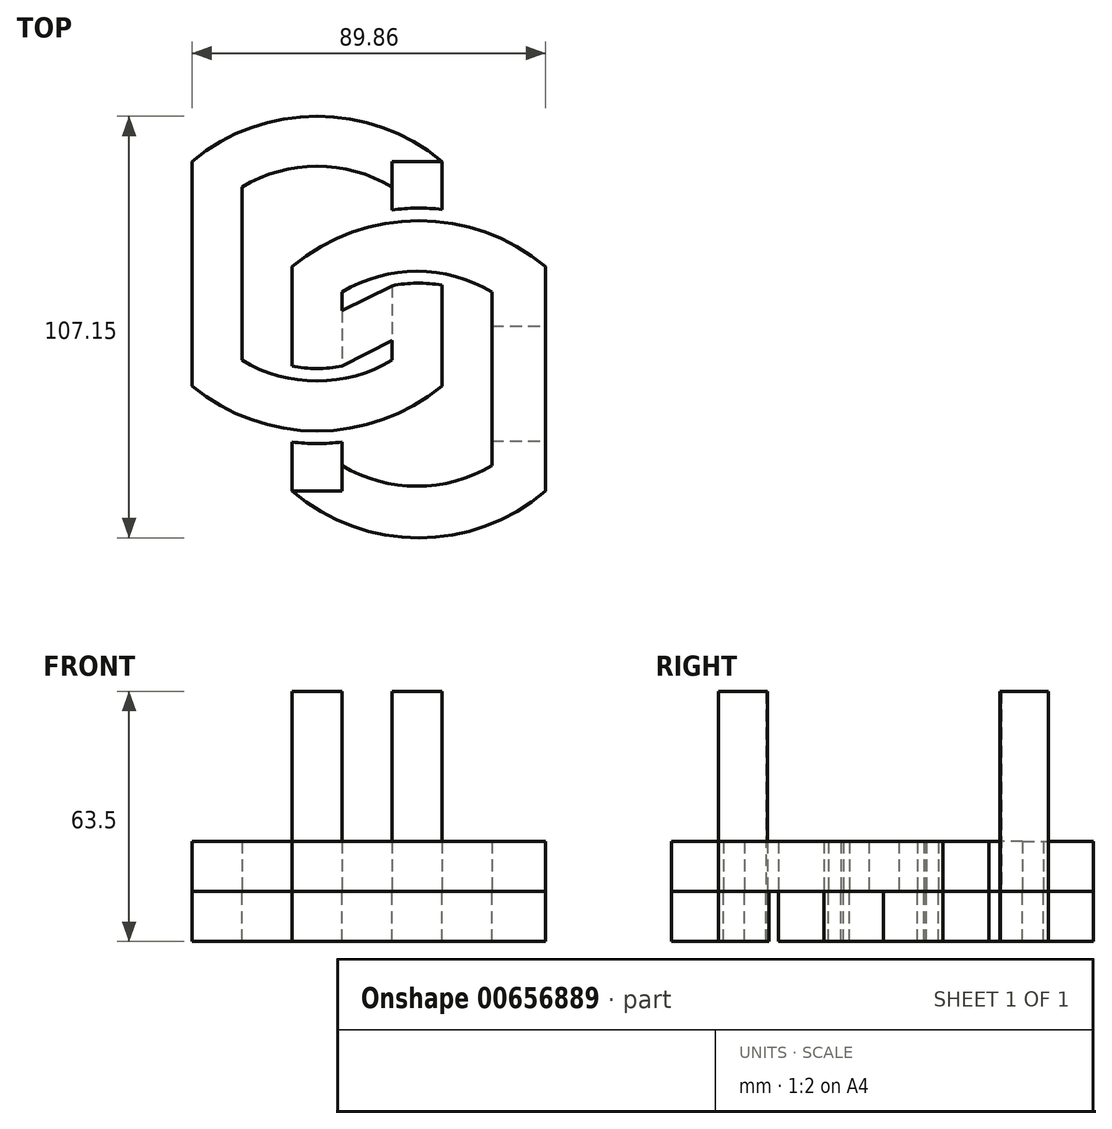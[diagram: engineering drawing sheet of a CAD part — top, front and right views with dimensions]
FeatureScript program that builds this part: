
annotation { "Feature Type Name" : "Feature", "Feature Type Description" : "" }
export const myFeature = defineFeature(function(context is Context, id is Id, definition is map)
    precondition{}
    {
        {
            var Q0;
            Q0=qCreatedBy(makeId("Top.planeOp"),FACE);
            var sketch = newSketch(context, id + "F0", { "sketchPlane" : qUnion([Q0])});
            skLineSegment(sketch, "E0.0", {"start": v(-60.44, 47.14) * mm, "end": v(-60.44, -9.85) * mm});
            skArc(sketch, "E1.0", {"start": v(-47.74, -3.35) * mm, "mid": v(-28.7, -8.66) * mm, "end": v(-9.64, -3.35) * mm});
            skArc(sketch, "E2.0", {"start": v(-60.44, -9.85) * mm, "mid": v(-28.7, -21.36) * mm, "end": v(3.06, -9.85) * mm});
            skArc(sketch, "E3.0", {"start": v(3.06, 47.14) * mm, "mid": v(-28.7, 58.65) * mm, "end": v(-60.44, 47.14) * mm});
            skArc(sketch, "E4.0", {"start": v(-9.64, 40.65) * mm, "mid": v(-28.7, 45.95) * mm, "end": v(-47.74, 40.65) * mm});
            skLineSegment(sketch, "E5.0", {"start": v(-47.74, 40.65) * mm, "end": v(-47.74, -3.35) * mm});
            skLineSegment(sketch, "E6.0", {"start": v(-9.64, 40.65) * mm, "end": v(-9.64, 34.84) * mm});
            skLineSegment(sketch, "E7.0", {"start": v(3.06, 47.14) * mm, "end": v(3.06, 34.96) * mm});
            skLineSegment(sketch, "E8.0.1.0", {"start": v(-35.05, 20.42) * mm, "end": v(-35.05, -4.88) * mm});
            skArc(sketch, "E8.0.1.1", {"start": v(-35.05, -36.58) * mm, "mid": v(-2.81, -48.5) * mm, "end": v(29.42, -36.58) * mm});
            skArc(sketch, "E8.0.1.2", {"start": v(-22.34, -30.07) * mm, "mid": v(-3.3, -35.38) * mm, "end": v(15.76, -30.07) * mm});
            skArc(sketch, "E8.0.1.5", {"start": v(15.76, 13.93) * mm, "mid": v(-3.3, 19.23) * mm, "end": v(-22.34, 13.93) * mm});
            skArc(sketch, "E8.0.1.6", {"start": v(29.42, 20.42) * mm, "mid": v(-2.81, 32.1) * mm, "end": v(-35.05, 20.42) * mm});
            skLineSegment(sketch, "E8.0.1.7", {"start": v(-22.34, 13.93) * mm, "end": v(-22.34, -4.88) * mm});
            skLineSegment(sketch, "E8.0.1.8", {"start": v(29.42, 20.42) * mm, "end": v(29.42, 5.28) * mm});
            skLineSegment(sketch, "E8.0.1.9", {"start": v(15.76, 13.93) * mm, "end": v(15.76, 5.28) * mm});
            skLineSegment(sketch, "E9", {"start": v(15.76, 5.28) * mm, "end": v(29.42, 5.28) * mm});
            skLineSegment(sketch, "E10", {"start": v(15.76, -23.85) * mm, "end": v(29.42, -23.85) * mm});
            skLineSegment(sketch, "E11.trimOffspring", {"start": v(15.76, -23.85) * mm, "end": v(15.76, -30.07) * mm});
            skLineSegment(sketch, "E12.trimOffspring", {"start": v(29.42, -23.85) * mm, "end": v(29.42, -36.58) * mm});
            skArc(sketch, "E13.0", {"start": v(3.06, 34.96) * mm, "mid": v(-3.3, 35.28) * mm, "end": v(-9.64, 34.84) * mm});
            skArc(sketch, "E14.0", {"start": v(3.06, 15.72) * mm, "mid": v(-3.3, 16.23) * mm, "end": v(-9.64, 15.54) * mm});
            skLineSegment(sketch, "E15.trimOffspring", {"start": v(3.06, 15.72) * mm, "end": v(3.06, -9.85) * mm});
            skLineSegment(sketch, "E16.trimOffspring", {"start": v(-9.64, 15.54) * mm, "end": v(-9.64, -3.35) * mm});
            skArc(sketch, "E17.0", {"start": v(-35.05, -4.88) * mm, "mid": v(-28.7, -5.48) * mm, "end": v(-22.34, -4.88) * mm});
            skArc(sketch, "E18.0", {"start": v(-35.05, -24.15) * mm, "mid": v(-28.7, -24.53) * mm, "end": v(-22.34, -24.15) * mm});
            skLineSegment(sketch, "E19.trimOffspring", {"start": v(-35.05, -24.15) * mm, "end": v(-35.05, -36.58) * mm});
            skLineSegment(sketch, "E20.trimOffspring", {"start": v(-22.34, -24.15) * mm, "end": v(-22.34, -30.07) * mm});
            skLineSegment(sketch, "E21", {"start": v(-22.34, 9.21) * mm, "end": v(-9.64, 15.54) * mm});
            skLineSegment(sketch, "E22", {"start": v(-22.34, -4.88) * mm, "end": v(-9.64, 1.64) * mm});
            skLineSegment(sketch, "E23.left", {"start": v(15.76, -23.85) * mm, "end": v(15.76, 5.28) * mm});
            skLineSegment(sketch, "E23.right", {"start": v(29.42, -23.85) * mm, "end": v(29.42, 5.28) * mm});
            skLineSegment(sketch, "E24.top", {"start": v(-22.34, -36.58) * mm, "end": v(-35.05, -36.58) * mm});
            skLineSegment(sketch, "E24.left", {"start": v(-22.34, -24.15) * mm, "end": v(-22.34, -36.58) * mm});
            skLineSegment(sketch, "E25.top", {"start": v(-9.64, 47.14) * mm, "end": v(3.06, 47.14) * mm});
            skLineSegment(sketch, "E25.left", {"start": v(-9.64, 34.84) * mm, "end": v(-9.64, 47.14) * mm});
            skLineSegment(sketch, "E25.right", {"start": v(3.06, 34.84) * mm, "end": v(3.06, 47.14) * mm});
            skSolve(sketch);
        }
        {
            var Q0;
            Q0=makeQuery(id+"F0.imprint","IMPRINT",FACE,{"disambiguationData":[TD([[makeQuery(id+"F0.imprint","IMPRINT",EDGE,{"derivedFrom":sQuery(id+"F0.wireOp",EDGE,"E0.0")}),1.0]])]});
            var Q1;
            Q1=makeQuery(id+"F0.imprint","IMPRINT",FACE,{"disambiguationData":[TD([[makeQuery(id+"F0.imprint","IMPRINT",EDGE,{"derivedFrom":sQuery(id+"F0.wireOp",EDGE,"E8.0.1.0")}),1.0]])]});
            var Q2;
            Q2=makeQuery(id+"F0.imprint","IMPRINT",FACE,{"disambiguationData":[TD([[makeQuery(id+"F0.imprint","IMPRINT",EDGE,{"derivedFrom":sQuery(id+"F0.wireOp",EDGE,"E8.0.1.1")}),1.0]])]});
            var Q3;
            {var subQ2=sQuery(id+"F0.wireOp",EDGE,"E18.0");Q3=makeQuery(id+"F0.imprint","IMPRINT",FACE,{"disambiguationData":[TD([[makeQuery(id+"F0.imprint","IMPRINT",EDGE,{"derivedFrom":subQ2}),-1.0]])]});}
            var Q4;
            {var subQ2=sQuery(id+"F0.wireOp",EDGE,"E13.0");Q4=makeQuery(id+"F0.imprint","IMPRINT",FACE,{"disambiguationData":[TD([[makeQuery(id+"F0.imprint","IMPRINT",EDGE,{"derivedFrom":subQ2}),-1.0]])]});}
            extrude(context, id + "F1", {"entities" : qUnion([Q0, Q1, Q2, Q3, Q4]), "depth" : -12.7 * mm, "offsetDistance" : 25.4 * mm});
        }
        {
            var Q0;
            {var subQ2=sQuery(id+"F0.wireOp",EDGE,"E13.0");Q0=makeQuery(id+"F0.imprint","IMPRINT",FACE,{"disambiguationData":[TD([[makeQuery(id+"F0.imprint","IMPRINT",EDGE,{"derivedFrom":subQ2}),-1.0]])]});}
            var Q1;
            {var subQ2=sQuery(id+"F0.wireOp",EDGE,"E18.0");Q1=makeQuery(id+"F0.imprint","IMPRINT",FACE,{"disambiguationData":[TD([[makeQuery(id+"F0.imprint","IMPRINT",EDGE,{"derivedFrom":subQ2}),-1.0]])]});}
            extrude(context, id + "F2", {"entities" : qUnion([Q0, Q1]), "depth" : 50.8 * mm, "offsetDistance" : 25.4 * mm});
        }
        {
            var Q0;
            Q0=makeQuery(id+"F0.imprint","IMPRINT",FACE,{"disambiguationData":[TD([[makeQuery(id+"F0.imprint","IMPRINT",EDGE,{"derivedFrom":sQuery(id+"F0.wireOp",EDGE,"E0.0")}),1.0]])]});
            var Q1;
            Q1=makeQuery(id+"F0.imprint","IMPRINT",FACE,{"disambiguationData":[TD([[makeQuery(id+"F0.imprint","IMPRINT",EDGE,{"derivedFrom":sQuery(id+"F0.wireOp",EDGE,"E8.0.1.0")}),1.0]])]});
            var Q2;
            {var subQ2=sQuery(id+"F0.wireOp",EDGE,"E21");Q2=makeQuery(id+"F0.imprint","IMPRINT",FACE,{"disambiguationData":[TD([[makeQuery(id+"F0.imprint","IMPRINT",EDGE,{"derivedFrom":subQ2}),-1.0]])]});}
            var Q3;
            Q3=makeQuery(id+"F0.imprint","IMPRINT",FACE,{"disambiguationData":[TD([[makeQuery(id+"F0.imprint","IMPRINT",EDGE,{"derivedFrom":sQuery(id+"F0.wireOp",EDGE,"E10")}),1.0]])]});
            var Q4;
            Q4=makeQuery(id+"F0.imprint","IMPRINT",FACE,{"disambiguationData":[TD([[makeQuery(id+"F0.imprint","IMPRINT",EDGE,{"derivedFrom":sQuery(id+"F0.wireOp",EDGE,"E8.0.1.1")}),1.0]])]});
            extrude(context, id + "F3", {"entities" : qUnion([Q0, Q1, Q2, Q3, Q4]), "depth" : 12.7 * mm, "offsetDistance" : 25.4 * mm});
        }
    });
